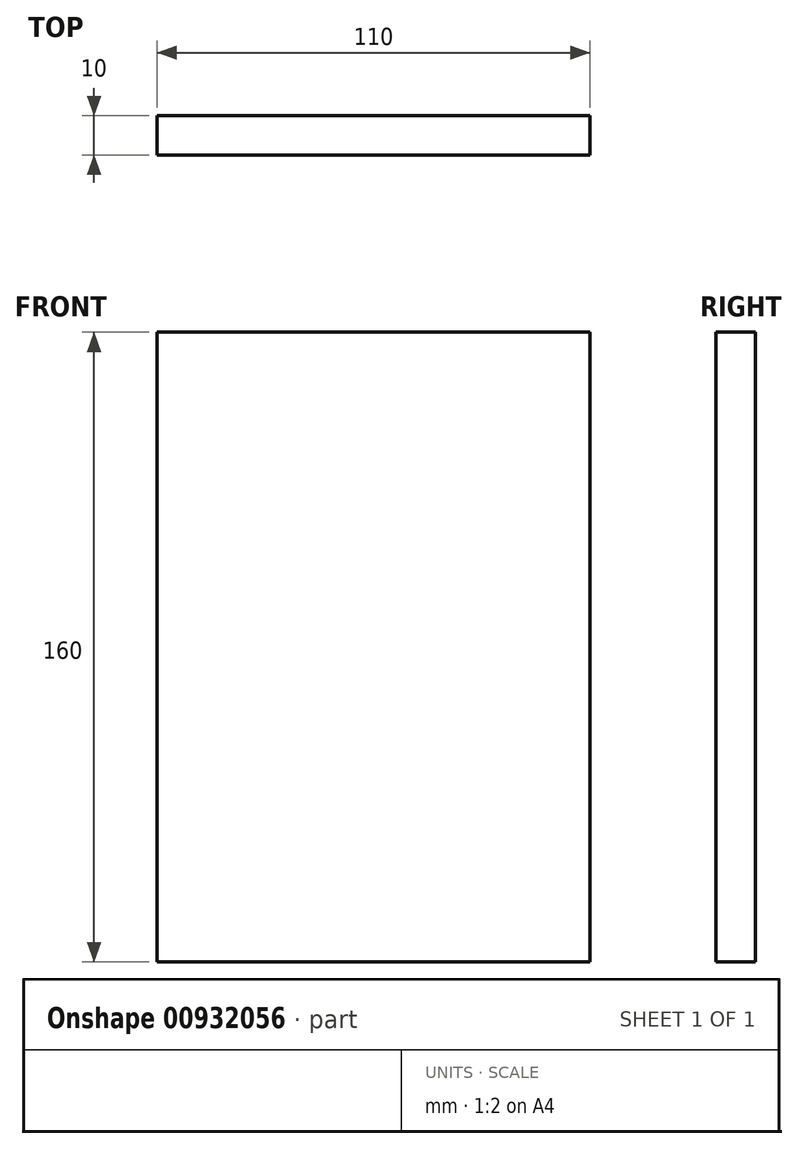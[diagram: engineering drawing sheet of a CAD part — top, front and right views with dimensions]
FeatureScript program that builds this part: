
annotation { "Feature Type Name" : "Feature", "Feature Type Description" : "" }
export const myFeature = defineFeature(function(context is Context, id is Id, definition is map)
    precondition{}
    {
        {
            var Q0;
            Q0=qCreatedBy(makeId("Front.planeOp"),FACE);
            var sketch = newSketch(context, id + "F0", { "sketchPlane" : qUnion([Q0])});
            skLineSegment(sketch, "E0.bottom", {"start": v(0, 0) * mm, "end": v(110, 0) * mm});
            skLineSegment(sketch, "E0.top", {"start": v(0, 160) * mm, "end": v(110, 160) * mm});
            skLineSegment(sketch, "E0.left", {"start": v(0, 0) * mm, "end": v(0, 160) * mm});
            skLineSegment(sketch, "E0.right", {"start": v(110, 0) * mm, "end": v(110, 160) * mm});
            skSolve(sketch);
        }
        {
            var Q0;
            Q0=makeQuery(id+"F0.imprint","IMPRINT",FACE,{"disambiguationData":[TD([[makeQuery(id+"F0.imprint","IMPRINT",EDGE,{"derivedFrom":sQuery(id+"F0.wireOp",EDGE,"E0.bottom")}),1.0]])]});
            extrude(context, id + "F1", {"entities" : qUnion([Q0]), "depth" : 10 * mm, "offsetDistance" : 25 * mm});
        }
    });
